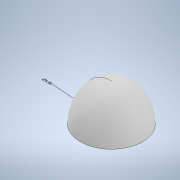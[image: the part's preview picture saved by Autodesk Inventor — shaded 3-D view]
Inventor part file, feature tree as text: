
AUTODESK INVENTOR PART (.ipt)
format: ipt  version: 2022 (Build 260153000, 153)  size: 239,104 bytes
history: native  units: in
note: dims shown in document units (in); Inventor stores cm internally (conversion verified against a paired STEP export)
features: other x2, revolve x1, thicken_offset x1, shell x1, sketch x1
ambient origin geometry x8: Origin, YZ Plane, XZ Plane, XY Plane, X Axis, Y Axis, Z Axis, Center Point
bodies: Solid1 (feature_tree)
feature tree (6):
  other  "Annotations"
  revolve  "Revolution1"  [1 undecoded]
  thicken_offset  "Thicken1"
  shell  "Shell1"  Thickness=1.03in
  sketch  "Sketch1"  dims[d3=90.0deg d6=1.03in d7=1.03in d8=0.75in d4=1.2713in d5=5.06in]
  other  "Diameter Dimension 1"
note: 1 required parameter value undecoded (feature->parameter linkage not recoverable at this tier; creation-order binding heuristic only, values carry confidence <= 0.55)
